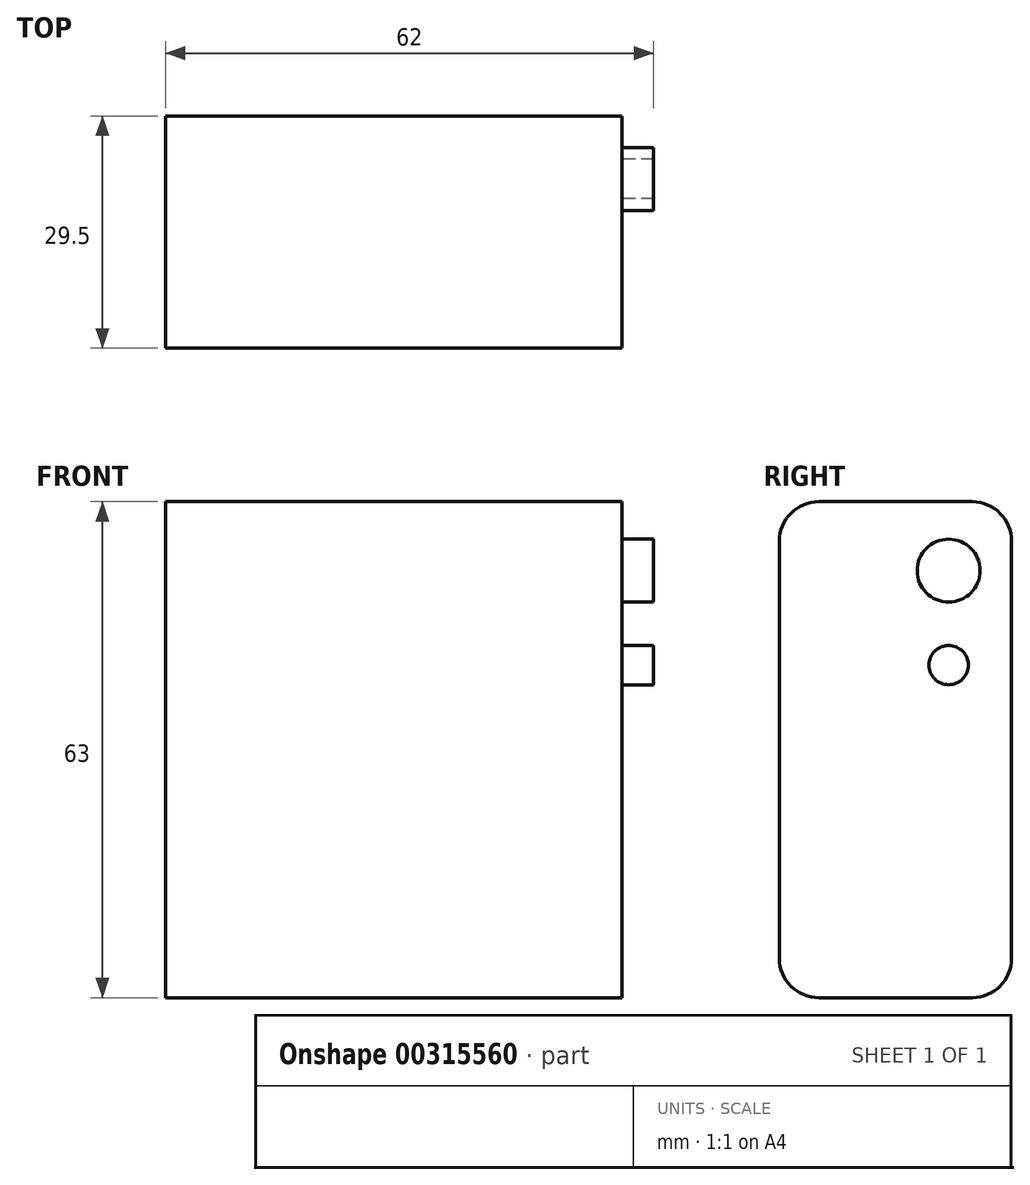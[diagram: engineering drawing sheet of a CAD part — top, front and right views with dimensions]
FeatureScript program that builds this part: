
annotation { "Feature Type Name" : "Feature", "Feature Type Description" : "" }
export const myFeature = defineFeature(function(context is Context, id is Id, definition is map)
    precondition{}
    {
        {
            var Q0;
            Q0=qCreatedBy(makeId("Front.planeOp"),FACE);
            var sketch = newSketch(context, id + "F0", { "sketchPlane" : qUnion([Q0])});
            skLineSegment(sketch, "E0.bottom", {"start": v(29, 31.5) * mm, "end": v(-29, 31.5) * mm});
            skLineSegment(sketch, "E0.top", {"start": v(29, -31.5) * mm, "end": v(-29, -31.5) * mm});
            skLineSegment(sketch, "E0.left", {"start": v(29, 31.5) * mm, "end": v(29, -31.5) * mm});
            skLineSegment(sketch, "E0.right", {"start": v(-29, 31.5) * mm, "end": v(-29, -31.5) * mm});
            skPoint(sketch, "E0.middle", {"position": v(0, 0) * mm});
            skSolve(sketch);
        }
        {
            var Q0;
            Q0 = qSketchRegion(id + "F0", true);
            extrude(context, id + "F1", {"entities" : qUnion([Q0]), "depth" : 29.5 * mm});
        }
        {
            var Q0;
            Q0=makeQuery(id+"F1.opExtrude","CAP_EDGE",EDGE,{"disambiguationData":[OSD([sQuery(id+"F0.wireOp",EDGE,"E0.bottom")])],"isStart":true});
            var Q1;
            Q1=makeQuery(id+"F1.opExtrude","CAP_EDGE",EDGE,{"disambiguationData":[OSD([sQuery(id+"F0.wireOp",EDGE,"E0.top")])],"isStart":true});
            var Q2;
            Q2=makeQuery(id+"F1.opExtrude","CAP_EDGE",EDGE,{"disambiguationData":[OSD([sQuery(id+"F0.wireOp",EDGE,"E0.top")])],"isStart":false});
            var Q3;
            Q3=makeQuery(id+"F1.opExtrude","CAP_EDGE",EDGE,{"disambiguationData":[OSD([sQuery(id+"F0.wireOp",EDGE,"E0.bottom")])],"isStart":false});
            fillet(context, id + "F2", {"entities" : qUnion([Q0, Q1, Q2, Q3]), "radius" : 5 * mm, "tangentPropagation" : true, "allowEdgeOverflow" : false});
        }
        {
            var Q0;
            Q0=makeQuery(id+"F1.opExtrude","SWEPT_FACE",FACE,{"disambiguationData":[OSD([sQuery(id+"F0.wireOp",EDGE,"E0.left")])]});
            var sketch = newSketch(context, id + "F3", { "sketchPlane" : qUnion([Q0])});
            skCircle(sketch, "E1", {"center": v(-8, 22.75) * mm, "radius": 4 * mm});
            skCircle(sketch, "E2", {"center": v(-8, 10.75) * mm, "radius": 2.5 * mm});
            skSolve(sketch);
        }
        {
            var Q0;
            Q0 = qSketchRegion(id + "F3", true);
            extrude(context, id + "F4", {"entities" : qUnion([Q0]), "operationType" : NewBodyOperationType.ADD, "depth" : 4 * mm});
        }
    });
